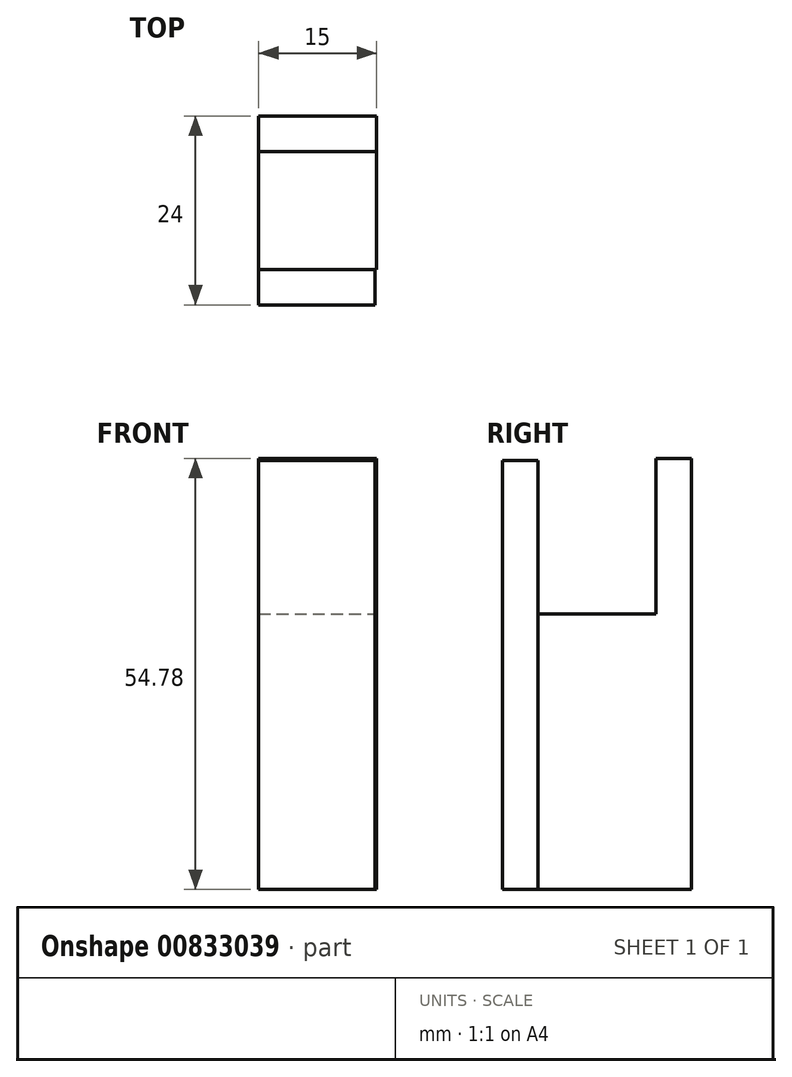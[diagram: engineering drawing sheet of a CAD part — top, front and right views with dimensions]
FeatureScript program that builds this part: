
annotation { "Feature Type Name" : "Feature", "Feature Type Description" : "" }
export const myFeature = defineFeature(function(context is Context, id is Id, definition is map)
    precondition{}
    {
        {
            var Q0;
            Q0=qCreatedBy(makeId("Top.planeOp"),FACE);
            var sketch = newSketch(context, id + "F0", { "sketchPlane" : qUnion([Q0])});
            skLineSegment(sketch, "E0.bottom", {"start": v(0, 0) * mm, "end": v(15, 0) * mm});
            skLineSegment(sketch, "E0.top", {"start": v(0, 15) * mm, "end": v(15, 15) * mm});
            skLineSegment(sketch, "E0.left", {"start": v(0, 0) * mm, "end": v(0, 15) * mm});
            skLineSegment(sketch, "E0.right", {"start": v(15, 0) * mm, "end": v(15, 15) * mm});
            skSolve(sketch);
        }
        {
            var Q0;
            Q0 = qSketchRegion(id + "F0", true);
            extrude(context, id + "F1", {"entities" : qUnion([Q0]), "depth" : 35 * mm, "offsetDistance" : 25.4 * mm});
        }
        {
            var Q0;
            Q0=makeQuery(id+"F1.opExtrude","CAP_FACE",FACE,{"disambiguationData":[OSD([sQuery(id+"F0.wireOp",EDGE,"E0.bottom"),sQuery(id+"F0.wireOp",EDGE,"E0.top"),sQuery(id+"F0.wireOp",EDGE,"E0.left"),sQuery(id+"F0.wireOp",EDGE,"E0.right")])],"isStart":false});
            var sketch = newSketch(context, id + "F2", { "sketchPlane" : qUnion([Q0])});
            skLineSegment(sketch, "E1.bottom", {"start": v(0, 15) * mm, "end": v(-8.77, 15) * mm});
            skLineSegment(sketch, "E1.top", {"start": v(0, 0) * mm, "end": v(-8.77, 0) * mm});
            skLineSegment(sketch, "E1.left", {"start": v(0, 15) * mm, "end": v(0, 0) * mm});
            skLineSegment(sketch, "E1.right", {"start": v(-8.77, 15) * mm, "end": v(-8.77, 0) * mm});
            skLineSegment(sketch, "E2.bottom", {"start": v(15, 15) * mm, "end": v(23.55, 15) * mm});
            skLineSegment(sketch, "E2.top", {"start": v(15, 0) * mm, "end": v(23.55, 0) * mm});
            skLineSegment(sketch, "E2.left", {"start": v(15, 15) * mm, "end": v(15, 0) * mm});
            skLineSegment(sketch, "E2.right", {"start": v(23.55, 15) * mm, "end": v(23.55, 0) * mm});
            skSolve(sketch);
        }
        {
            var Q0;
            Q0=makeQuery(id+"F2.imprint","IMPRINT",FACE,{"disambiguationData":[TD([[makeQuery(id+"F2.imprint","IMPRINT",EDGE,{"derivedFrom":sQuery(id+"F2.wireOp",EDGE,"E2.bottom")}),-1.0]])]});
            var Q1;
            Q1=makeQuery(id+"F2.imprint","IMPRINT",FACE,{"disambiguationData":[TD([[makeQuery(id+"F2.imprint","IMPRINT",EDGE,{"derivedFrom":sQuery(id+"F2.wireOp",EDGE,"E1.bottom")}),1.0]])]});
            extrude(context, id + "F3", {"entities" : qUnion([Q0, Q1]), "depth" : 25.4 * mm, "offsetDistance" : 25.4 * mm});
        }
        {
            var Q0;
            Q0=makeQuery(id+"F1.opExtrude","SWEPT_FACE",FACE,{"disambiguationData":[OSD([sQuery(id+"F0.wireOp",EDGE,"E0.left")])]});
            var sketch = newSketch(context, id + "F4", { "sketchPlane" : qUnion([Q0])});
            skLineSegment(sketch, "E3.bottom", {"start": v(-15, 31.83) * mm, "end": v(0, 31.83) * mm});
            skLineSegment(sketch, "E3.top", {"start": v(-15, 35) * mm, "end": v(0, 35) * mm});
            skLineSegment(sketch, "E3.left", {"start": v(-15, 31.83) * mm, "end": v(-15, 35) * mm});
            skLineSegment(sketch, "E3.right", {"start": v(0, 31.83) * mm, "end": v(0, 35) * mm});
            skSolve(sketch);
        }
        {
            var Q0;
            Q0=makeQuery(id+"F3.opExtrude","SWEPT_BODY",BODY,{"disambiguationData":[OSD([sQuery(id+"F2.wireOp",EDGE,"E2.bottom"),sQuery(id+"F2.wireOp",EDGE,"E2.top"),sQuery(id+"F2.wireOp",EDGE,"E2.left"),sQuery(id+"F2.wireOp",EDGE,"E2.right")])]});
            var Q1;
            Q1=makeQuery(id+"F3.opExtrude","SWEPT_BODY",BODY,{"disambiguationData":[OSD([sQuery(id+"F2.wireOp",EDGE,"E1.bottom"),sQuery(id+"F2.wireOp",EDGE,"E1.top"),sQuery(id+"F2.wireOp",EDGE,"E1.left"),sQuery(id+"F2.wireOp",EDGE,"E1.right")])]});
            deleteBodies(context, id + "F5", {"entities" : qUnion([Q0, Q1])});
        }
        {
            var Q0;
            Q0=makeQuery(id+"F1.opExtrude","SWEPT_FACE",FACE,{"disambiguationData":[OSD([sQuery(id+"F0.wireOp",EDGE,"E0.top")])]});
            var sketch = newSketch(context, id + "F6", { "sketchPlane" : qUnion([Q0])});
            skLineSegment(sketch, "E4.bottom", {"start": v(-15, 0) * mm, "end": v(0, 0) * mm});
            skLineSegment(sketch, "E4.top", {"start": v(-15, 54.78) * mm, "end": v(0, 54.78) * mm});
            skLineSegment(sketch, "E4.left", {"start": v(-15, 0) * mm, "end": v(-15, 54.78) * mm});
            skLineSegment(sketch, "E4.right", {"start": v(0, 0) * mm, "end": v(0, 54.78) * mm});
            skSolve(sketch);
        }
        {
            var Q0;
            Q0 = qSketchRegion(id + "F6", true);
            extrude(context, id + "F7", {"entities" : qUnion([Q0]), "operationType" : NewBodyOperationType.ADD, "depth" : 4.5 * mm, "offsetDistance" : 25.4 * mm});
        }
        {
            var Q0;
            Q0=makeQuery(id+"F1.opExtrude","SWEPT_FACE",FACE,{"disambiguationData":[OSD([sQuery(id+"F0.wireOp",EDGE,"E0.bottom")])]});
            var sketch = newSketch(context, id + "F8", { "sketchPlane" : qUnion([Q0])});
            skLineSegment(sketch, "E5.bottom", {"start": v(0, 0) * mm, "end": v(14.79, 0) * mm});
            skLineSegment(sketch, "E5.top", {"start": v(0, 54.53) * mm, "end": v(14.79, 54.53) * mm});
            skLineSegment(sketch, "E5.left", {"start": v(0, 0) * mm, "end": v(0, 54.53) * mm});
            skLineSegment(sketch, "E5.right", {"start": v(14.79, 0) * mm, "end": v(14.79, 54.53) * mm});
            skSolve(sketch);
        }
        {
            var Q0;
            Q0 = qSketchRegion(id + "F8", true);
            extrude(context, id + "F9", {"entities" : qUnion([Q0]), "operationType" : NewBodyOperationType.ADD, "depth" : 4.5 * mm, "offsetDistance" : 25.4 * mm});
        }
    });
